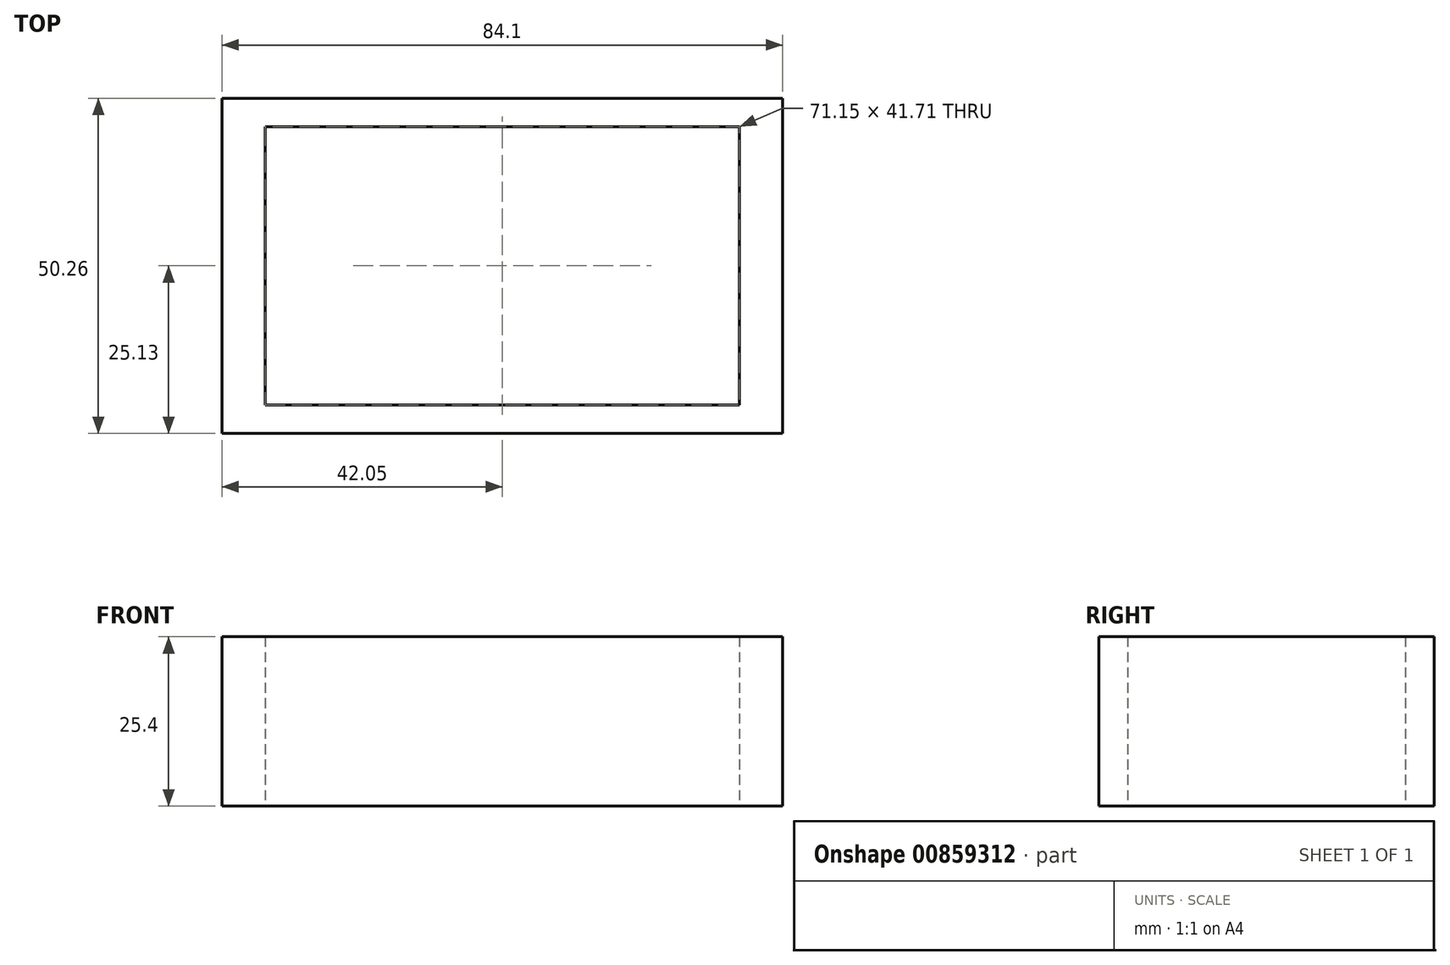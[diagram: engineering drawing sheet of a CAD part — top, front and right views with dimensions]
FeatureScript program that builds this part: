
annotation { "Feature Type Name" : "Feature", "Feature Type Description" : "" }
export const myFeature = defineFeature(function(context is Context, id is Id, definition is map)
    precondition{}
    {
        {
            var Q0;
            Q0=qCreatedBy(makeId("Top.planeOp"),FACE);
            var sketch = newSketch(context, id + "F0", { "sketchPlane" : qUnion([Q0])});
            skLineSegment(sketch, "E0.bottom", {"start": v(-122.22, 60.23) * mm, "end": v(122.22, 60.23) * mm});
            skLineSegment(sketch, "E0.top", {"start": v(-122.22, -60.23) * mm, "end": v(122.22, -60.23) * mm});
            skLineSegment(sketch, "E0.left", {"start": v(-122.22, 60.23) * mm, "end": v(-122.22, -60.23) * mm});
            skLineSegment(sketch, "E0.right", {"start": v(122.22, 60.23) * mm, "end": v(122.22, -60.23) * mm});
            skPoint(sketch, "E0.middle", {"position": v(0, 0) * mm});
            skSolve(sketch);
        }
        {
            var Q0;
            Q0=makeQuery(id+"F0.imprint","IMPRINT",FACE,{"disambiguationData":[TD([[makeQuery(id+"F0.imprint","IMPRINT",EDGE,{"derivedFrom":sQuery(id+"F0.wireOp",EDGE,"E0.bottom")}),-1.0]])]});
            var sketch = newSketch(context, id + "F1", { "sketchPlane" : qUnion([Q0])});
            skLineSegment(sketch, "E1.bottom", {"start": v(42.05, -25.13) * mm, "end": v(-42.05, -25.13) * mm});
            skLineSegment(sketch, "E1.top", {"start": v(42.05, 25.13) * mm, "end": v(-42.05, 25.13) * mm});
            skLineSegment(sketch, "E1.left", {"start": v(42.05, -25.13) * mm, "end": v(42.05, 25.13) * mm});
            skLineSegment(sketch, "E1.right", {"start": v(-42.05, -25.13) * mm, "end": v(-42.05, 25.13) * mm});
            skPoint(sketch, "E1.middle", {"position": v(0, 0) * mm});
            skLineSegment(sketch, "E2.bottom", {"start": v(35.57, -20.85) * mm, "end": v(-35.57, -20.85) * mm});
            skLineSegment(sketch, "E2.top", {"start": v(35.57, 20.85) * mm, "end": v(-35.57, 20.85) * mm});
            skLineSegment(sketch, "E2.left", {"start": v(35.57, -20.85) * mm, "end": v(35.57, 20.85) * mm});
            skLineSegment(sketch, "E2.right", {"start": v(-35.57, -20.85) * mm, "end": v(-35.57, 20.85) * mm});
            skSolve(sketch);
        }
        {
            var Q0;
            Q0 = qSketchRegion(id + "F1", true);
            extrude(context, id + "F2", {"entities" : qUnion([Q0]), "depth" : 25.4 * mm, "offsetDistance" : 25.4 * mm});
        }
    });
